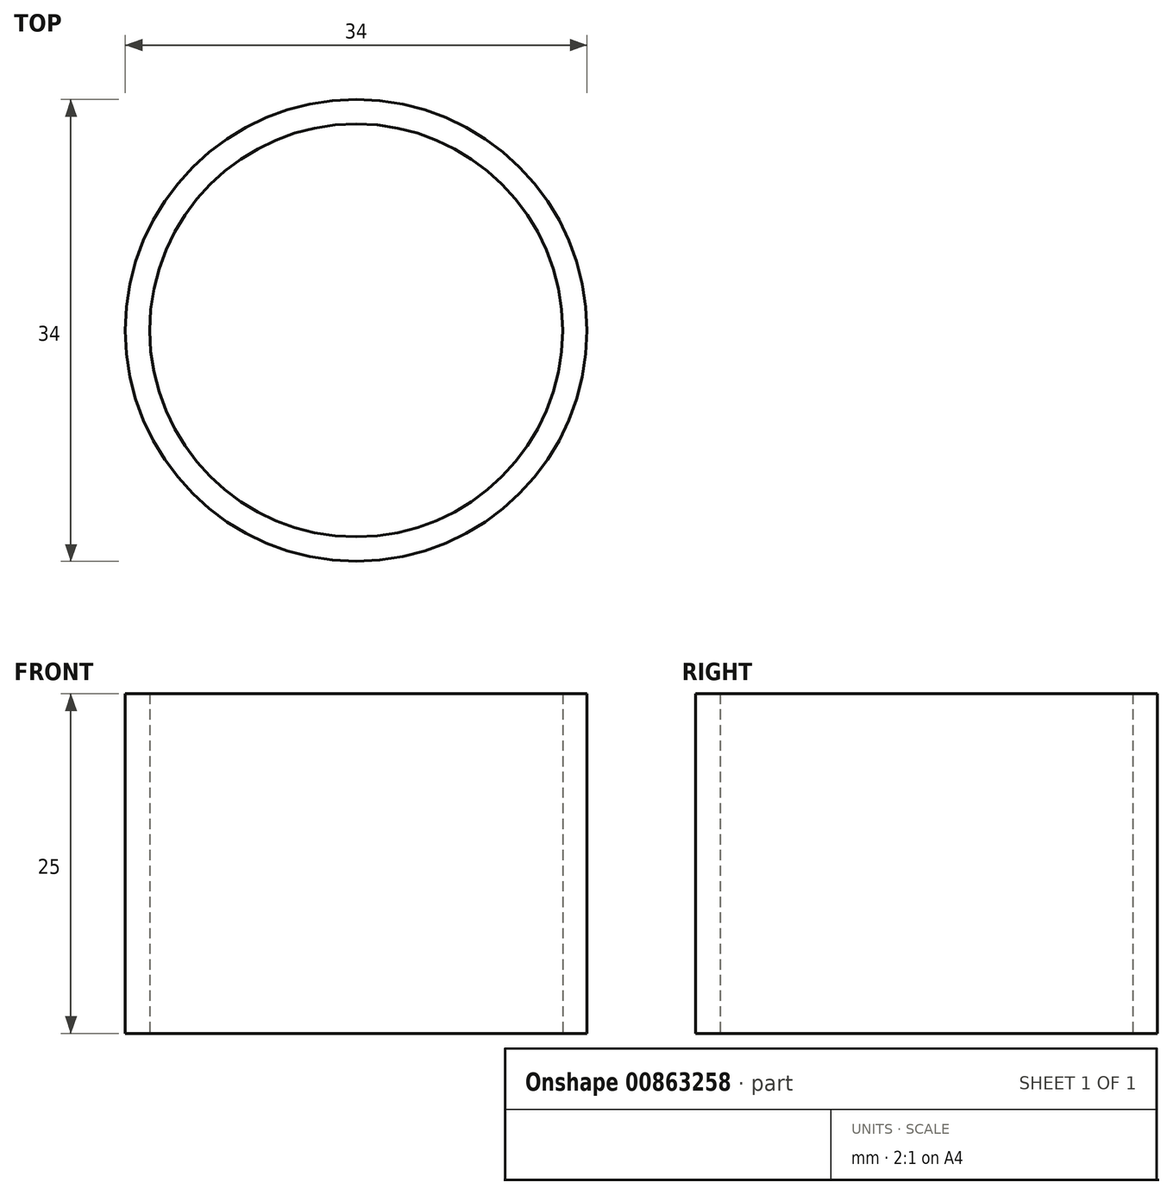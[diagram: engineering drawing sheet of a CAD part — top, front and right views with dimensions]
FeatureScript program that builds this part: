
annotation { "Feature Type Name" : "Feature", "Feature Type Description" : "" }
export const myFeature = defineFeature(function(context is Context, id is Id, definition is map)
    precondition{}
    {
        {
            var Q0;
            Q0=qCreatedBy(makeId("Top.planeOp"),FACE);
            var sketch = newSketch(context, id + "F0", { "sketchPlane" : qUnion([Q0])});
            skCircle(sketch, "E0", {"center": v(0, 0) * mm, "radius": 17 * mm});
            skCircle(sketch, "E1.0", {"center": v(0, 0) * mm, "radius": 15.2 * mm});
            skSolve(sketch);
        }
        {
            var Q0;
            Q0=makeQuery(id+"F0.imprint","IMPRINT",FACE,{"disambiguationData":[TD([[makeQuery(id+"F0.imprint","IMPRINT",EDGE,{"derivedFrom":sQuery(id+"F0.wireOp",EDGE,"E0")}),1.0]])]});
            extrude(context, id + "F1", {"entities" : qUnion([Q0]), "depth" : 25 * mm, "offsetDistance" : 25 * mm});
        }
    });
